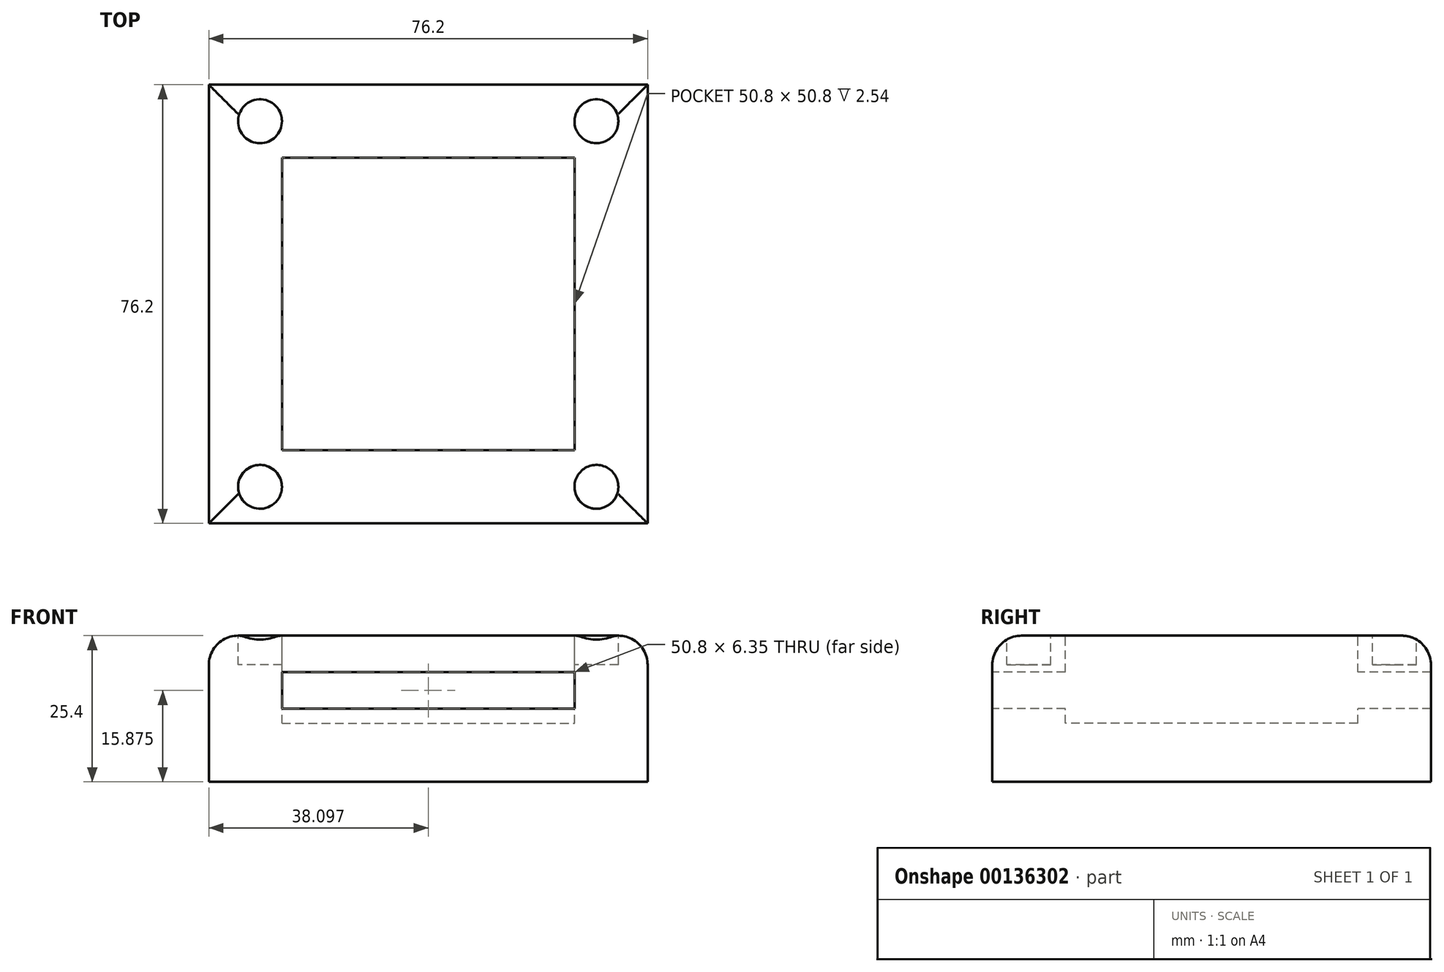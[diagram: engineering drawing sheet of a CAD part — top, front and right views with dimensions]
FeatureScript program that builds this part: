
annotation { "Feature Type Name" : "Feature", "Feature Type Description" : "" }
export const myFeature = defineFeature(function(context is Context, id is Id, definition is map)
    precondition{}
    {
        {
            var Q0;
            Q0=qCreatedBy(makeId("Top.planeOp"),FACE);
            var sketch = newSketch(context, id + "F0", { "sketchPlane" : qUnion([Q0])});
            skLineSegment(sketch, "E0.bottom", {"start": v(-28.13, 39.36) * mm, "end": v(48.07, 39.36) * mm});
            skLineSegment(sketch, "E0.top", {"start": v(-28.13, -36.84) * mm, "end": v(48.07, -36.84) * mm});
            skLineSegment(sketch, "E0.left", {"start": v(-28.13, 39.36) * mm, "end": v(-28.13, -36.84) * mm});
            skLineSegment(sketch, "E0.right", {"start": v(48.07, 39.36) * mm, "end": v(48.07, -36.84) * mm});
            skSolve(sketch);
        }
        {
            var Q0;
            Q0=makeQuery(id+"F0.imprint","IMPRINT",FACE,{"disambiguationData":[TD([[makeQuery(id+"F0.imprint","IMPRINT",EDGE,{"derivedFrom":sQuery(id+"F0.wireOp",EDGE,"E0.bottom")}),-1.0]])]});
            extrude(context, id + "F1", {"entities" : qUnion([Q0]), "depth" : 25.4 * mm});
        }
        {
            var Q0;
            Q0=makeQuery(id+"F1.opExtrude","SWEPT_FACE",FACE,{"disambiguationData":[OSD([sQuery(id+"F0.wireOp",EDGE,"E0.top")])]});
            var sketch = newSketch(context, id + "F2", { "sketchPlane" : qUnion([Q0])});
            skLineSegment(sketch, "E1.bottom", {"start": v(-15.43, 19.05) * mm, "end": v(35.37, 19.05) * mm});
            skLineSegment(sketch, "E1.top", {"start": v(-15.43, 12.7) * mm, "end": v(35.37, 12.7) * mm});
            skLineSegment(sketch, "E1.left", {"start": v(-15.43, 19.05) * mm, "end": v(-15.43, 12.7) * mm});
            skLineSegment(sketch, "E1.right", {"start": v(35.37, 19.05) * mm, "end": v(35.37, 12.7) * mm});
            skSolve(sketch);
        }
        {
            var Q0;
            Q0 = qSketchRegion(id + "F2", true);
            extrude(context, id + "F3", {"entities" : qUnion([Q0]), "operationType" : NewBodyOperationType.REMOVE, "endBound" : BoundingType.THROUGH_ALL, "oppositeDirection" : true, "depth" : 25.4 * mm});
        }
        {
            var Q0;
            Q0=makeQuery(id+"F1.opExtrude","CAP_FACE",FACE,{"disambiguationData":[OSD([sQuery(id+"F0.wireOp",EDGE,"E0.bottom"),sQuery(id+"F0.wireOp",EDGE,"E0.top"),sQuery(id+"F0.wireOp",EDGE,"E0.left"),sQuery(id+"F0.wireOp",EDGE,"E0.right")])],"isStart":false});
            var sketch = newSketch(context, id + "F4", { "sketchPlane" : qUnion([Q0])});
            skLineSegment(sketch, "E2.bottom", {"start": v(-15.43, 26.66) * mm, "end": v(35.37, 26.66) * mm});
            skLineSegment(sketch, "E2.top", {"start": v(-15.43, -24.14) * mm, "end": v(35.37, -24.14) * mm});
            skLineSegment(sketch, "E2.left", {"start": v(-15.43, 26.66) * mm, "end": v(-15.43, -24.14) * mm});
            skLineSegment(sketch, "E2.right", {"start": v(35.37, 26.66) * mm, "end": v(35.37, -24.14) * mm});
            skSolve(sketch);
        }
        {
            var Q0;
            Q0=makeQuery(id+"F4.imprint","IMPRINT",FACE,{"disambiguationData":[TD([[makeQuery(id+"F4.imprint","IMPRINT",EDGE,{"derivedFrom":sQuery(id+"F4.wireOp",EDGE,"E2.bottom")}),-1.0]])]});
            extrude(context, id + "F5", {"entities" : qUnion([Q0]), "operationType" : NewBodyOperationType.REMOVE, "oppositeDirection" : true, "depth" : 15.24 * mm});
        }
        {
            var Q0;
            Q0=makeQuery(id+"F4.imprint","IMPRINT",FACE,{"disambiguationData":[TD([[makeQuery(id+"F4.imprint","IMPRINT",EDGE,{"derivedFrom":sQuery(id+"F4.wireOp",EDGE,"E2.bottom")}),1.0]])]});
            var sketch = newSketch(context, id + "F6", { "sketchPlane" : qUnion([Q0])});
            skCircle(sketch, "E3", {"center": v(-19.24, 33.01) * mm, "radius": 3.81 * mm});
            skCircle(sketch, "E4", {"center": v(39.18, 33.01) * mm, "radius": 3.81 * mm});
            skCircle(sketch, "E5", {"center": v(-19.24, -30.49) * mm, "radius": 3.81 * mm});
            skCircle(sketch, "E6", {"center": v(39.18, -30.49) * mm, "radius": 3.81 * mm});
            skSolve(sketch);
        }
        {
            var Q0;
            Q0 = qSketchRegion(id + "F6", true);
            extrude(context, id + "F7", {"entities" : qUnion([Q0]), "operationType" : NewBodyOperationType.REMOVE, "oppositeDirection" : true, "depth" : 5.08 * mm});
        }
        {
            var Q0;
            Q0=makeQuery(id+"F1.opExtrude","CAP_EDGE",EDGE,{"disambiguationData":[OSD([sQuery(id+"F0.wireOp",EDGE,"E0.right")])],"isStart":false});
            var Q1;
            Q1=makeQuery(id+"F1.opExtrude","CAP_EDGE",EDGE,{"disambiguationData":[OSD([sQuery(id+"F0.wireOp",EDGE,"E0.top")])],"isStart":false});
            var Q2;
            Q2=makeQuery(id+"F1.opExtrude","CAP_EDGE",EDGE,{"disambiguationData":[OSD([sQuery(id+"F0.wireOp",EDGE,"E0.left")])],"isStart":false});
            var Q3;
            Q3=makeQuery(id+"F1.opExtrude","CAP_EDGE",EDGE,{"disambiguationData":[OSD([sQuery(id+"F0.wireOp",EDGE,"E0.bottom")])],"isStart":false});
            fillet(context, id + "F8", {"entities" : qUnion([Q0, Q1, Q2, Q3]), "radius" : 5.08 * mm, "tangentPropagation" : true, "allowEdgeOverflow" : false});
        }
    });
